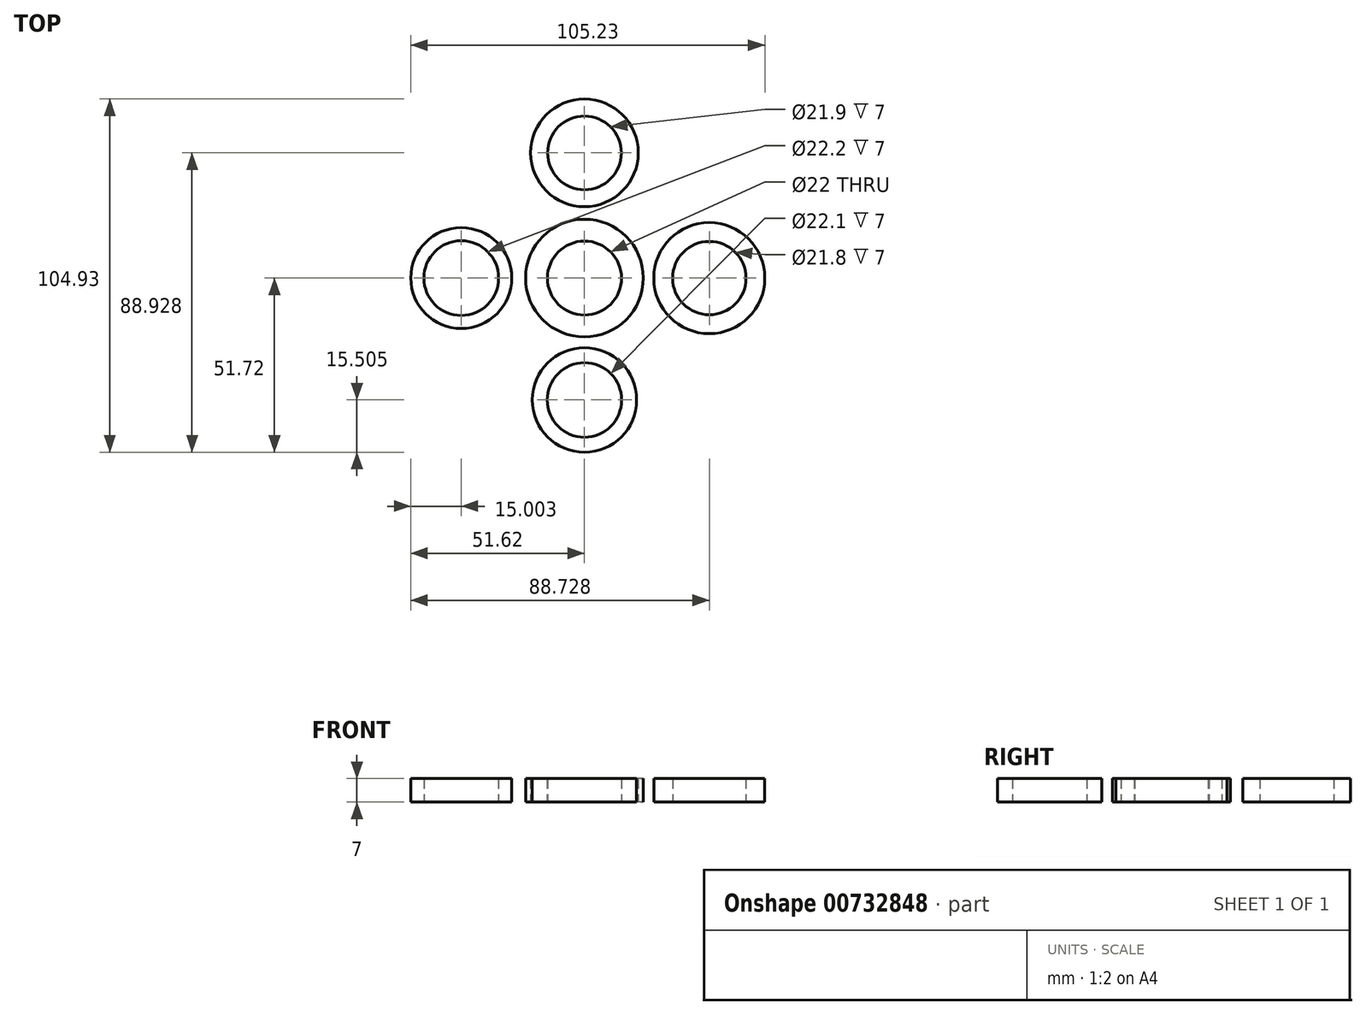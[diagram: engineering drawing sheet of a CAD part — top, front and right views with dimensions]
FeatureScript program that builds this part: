
annotation { "Feature Type Name" : "Feature", "Feature Type Description" : "" }
export const myFeature = defineFeature(function(context is Context, id is Id, definition is map)
    precondition{}
    {
        {
            var Q0;
            Q0=qCreatedBy(makeId("Top.planeOp"),FACE);
            var sketch = newSketch(context, id + "F0", { "sketchPlane" : qUnion([Q0])});
            skCircle(sketch, "E0", {"center": v(0, 0) * mm, "radius": 11 * mm});
            skCircle(sketch, "E1", {"center": v(0, 0) * mm, "radius": 17.5 * mm});
            skCircle(sketch, "E2", {"center": v(-36.62, 0) * mm, "radius": 11.1 * mm});
            skCircle(sketch, "E3", {"center": v(-36.62, 0) * mm, "radius": 15 * mm});
            skCircle(sketch, "E4", {"center": v(37.1, 0) * mm, "radius": 16.5 * mm});
            skCircle(sketch, "E5", {"center": v(37.1, 0) * mm, "radius": 10.9 * mm});
            skCircle(sketch, "E6", {"center": v(0, 37.2) * mm, "radius": 10.95 * mm});
            skCircle(sketch, "E7", {"center": v(0, 37.2) * mm, "radius": 16 * mm});
            skCircle(sketch, "E8", {"center": v(0, -36.22) * mm, "radius": 11.05 * mm});
            skCircle(sketch, "E9", {"center": v(0, -36.22) * mm, "radius": 15.5 * mm});
            skSolve(sketch);
        }
        {
            var Q0;
            Q0=makeQuery(id+"F0.imprint","IMPRINT",FACE,{"disambiguationData":[TD([[makeQuery(id+"F0.imprint","IMPRINT",EDGE,{"derivedFrom":sQuery(id+"F0.wireOp",EDGE,"E6")}),-1.0]])]});
            var Q1;
            Q1=makeQuery(id+"F0.imprint","IMPRINT",FACE,{"disambiguationData":[TD([[makeQuery(id+"F0.imprint","IMPRINT",EDGE,{"derivedFrom":sQuery(id+"F0.wireOp",EDGE,"E0")}),-1.0]])]});
            var Q2;
            Q2=makeQuery(id+"F0.imprint","IMPRINT",FACE,{"disambiguationData":[TD([[makeQuery(id+"F0.imprint","IMPRINT",EDGE,{"derivedFrom":sQuery(id+"F0.wireOp",EDGE,"E2")}),-1.0]])]});
            var Q3;
            Q3=makeQuery(id+"F0.imprint","IMPRINT",FACE,{"disambiguationData":[TD([[makeQuery(id+"F0.imprint","IMPRINT",EDGE,{"derivedFrom":sQuery(id+"F0.wireOp",EDGE,"E8")}),-1.0]])]});
            var Q4;
            Q4=makeQuery(id+"F0.imprint","IMPRINT",FACE,{"disambiguationData":[TD([[makeQuery(id+"F0.imprint","IMPRINT",EDGE,{"derivedFrom":sQuery(id+"F0.wireOp",EDGE,"E4")}),1.0]])]});
            extrude(context, id + "F1", {"entities" : qUnion([Q0, Q1, Q2, Q3, Q4]), "depth" : 7 * mm, "offsetDistance" : 25 * mm});
        }
    });
